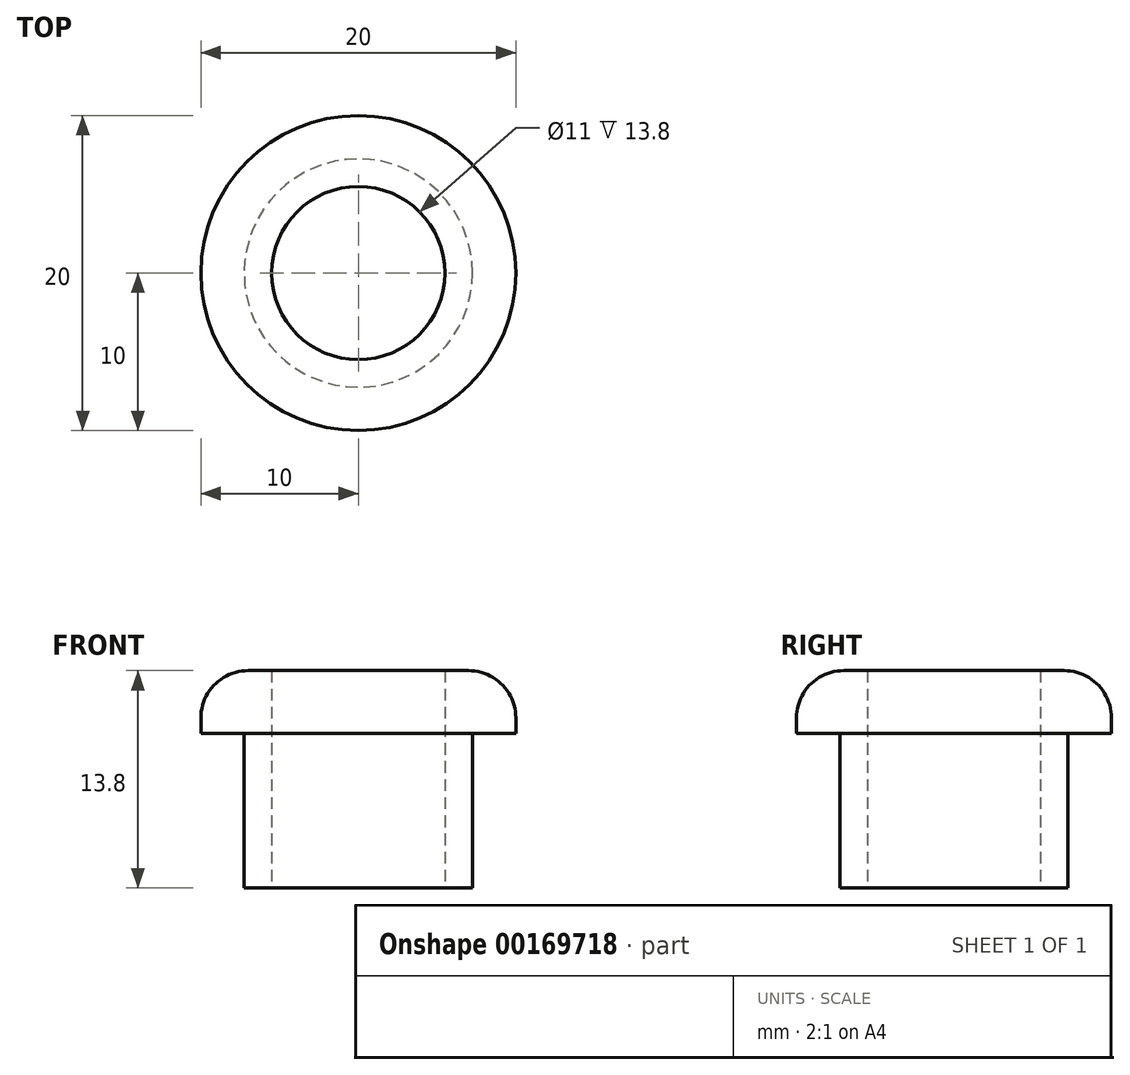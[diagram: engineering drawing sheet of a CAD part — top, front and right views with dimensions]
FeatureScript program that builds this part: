
annotation { "Feature Type Name" : "Feature", "Feature Type Description" : "" }
export const myFeature = defineFeature(function(context is Context, id is Id, definition is map)
    precondition{}
    {
        {
            var Q0;
            Q0=qCreatedBy(makeId("Top.planeOp"),FACE);
            var sketch = newSketch(context, id + "F0", { "sketchPlane" : qUnion([Q0])});
            skCircle(sketch, "E0", {"center": v(0, 0) * mm, "radius": 10 * mm});
            skCircle(sketch, "E1", {"center": v(0, 0) * mm, "radius": 7.25 * mm});
            skCircle(sketch, "E2", {"center": v(0, 0) * mm, "radius": 5.5 * mm});
            skSolve(sketch);
        }
        {
            var Q0;
            Q0=makeQuery(id+"F0.imprint","IMPRINT",FACE,{"disambiguationData":[TD([[makeQuery(id+"F0.imprint","IMPRINT",EDGE,{"derivedFrom":sQuery(id+"F0.wireOp",EDGE,"E0")}),1.0]])]});
            var Q1;
            Q1=makeQuery(id+"F0.imprint","IMPRINT",FACE,{"disambiguationData":[TD([[makeQuery(id+"F0.imprint","IMPRINT",EDGE,{"derivedFrom":sQuery(id+"F0.wireOp",EDGE,"E1")}),1.0]])]});
            extrude(context, id + "F1", {"entities" : qUnion([Q0, Q1]), "depth" : 4 * mm});
        }
        {
            var Q0;
            Q0=makeQuery(id+"F1.opExtrude","CAP_EDGE",EDGE,{"disambiguationData":[OSD([sQuery(id+"F0.wireOp",EDGE,"E0")])],"isStart":false});
            fillet(context, id + "F2", {"entities" : qUnion([Q0]), "radius" : 3 * mm, "tangentPropagation" : true, "allowEdgeOverflow" : false});
        }
        {
            var Q0;
            Q0=makeQuery(id+"F0.imprint","IMPRINT",FACE,{"disambiguationData":[TD([[makeQuery(id+"F0.imprint","IMPRINT",EDGE,{"derivedFrom":sQuery(id+"F0.wireOp",EDGE,"E1")}),1.0]])]});
            extrude(context, id + "F3", {"entities" : qUnion([Q0]), "operationType" : NewBodyOperationType.ADD, "oppositeDirection" : true, "depth" : (5.8 + 4) * mm});
        }
    });
